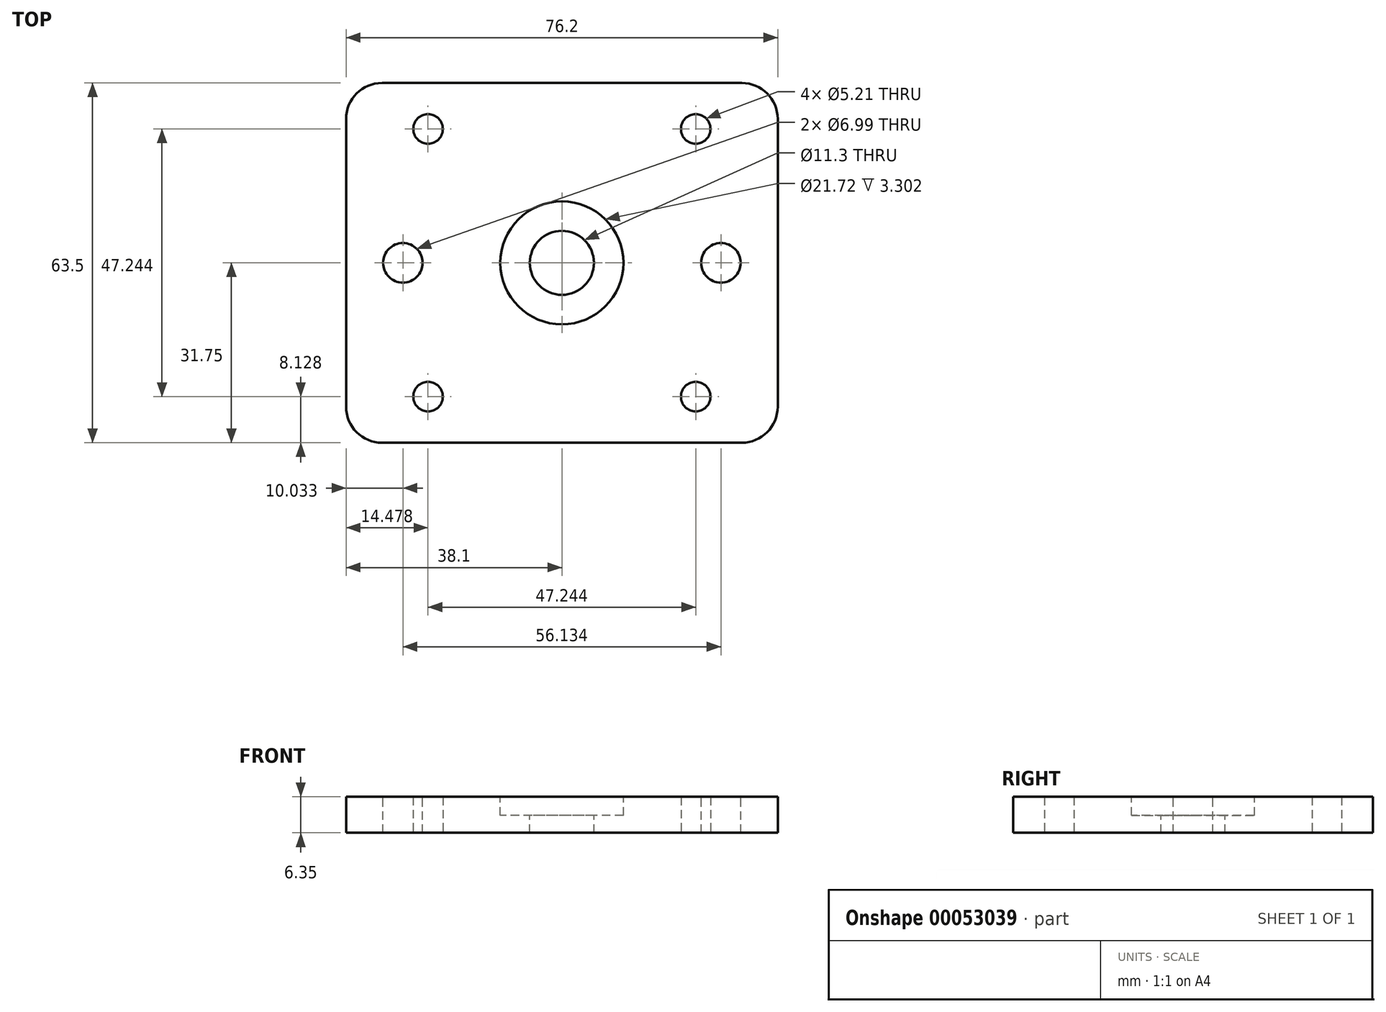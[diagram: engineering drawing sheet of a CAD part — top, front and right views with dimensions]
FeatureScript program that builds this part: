
annotation { "Feature Type Name" : "Feature", "Feature Type Description" : "" }
export const myFeature = defineFeature(function(context is Context, id is Id, definition is map)
    precondition{}
    {
        {
            var Q0;
            Q0=qCreatedBy(makeId("Top.planeOp"),FACE);
            var sketch = newSketch(context, id + "F0", { "sketchPlane" : qUnion([Q0])});
            skLineSegment(sketch, "E0.bottom", {"start": v(-23.62, 23.62) * mm, "end": v(23.62, 23.62) * mm});
            skLineSegment(sketch, "E0.top", {"start": v(-23.62, -23.62) * mm, "end": v(23.62, -23.62) * mm});
            skLineSegment(sketch, "E0.left", {"start": v(-23.62, 23.62) * mm, "end": v(-23.62, -23.62) * mm});
            skLineSegment(sketch, "E0.right", {"start": v(23.62, 23.62) * mm, "end": v(23.62, -23.62) * mm});
            skSolve(sketch);
        }
        {
            var Q0;
            Q0=qCreatedBy(makeId("Top.planeOp"),FACE);
            var sketch = newSketch(context, id + "F1", { "sketchPlane" : qUnion([Q0])});
            skLineSegment(sketch, "E1.bottom", {"start": v(-38.1, 31.75) * mm, "end": v(38.1, 31.75) * mm});
            skLineSegment(sketch, "E1.top", {"start": v(-38.1, -31.75) * mm, "end": v(38.1, -31.75) * mm});
            skLineSegment(sketch, "E1.left", {"start": v(-38.1, 31.75) * mm, "end": v(-38.1, -31.75) * mm});
            skLineSegment(sketch, "E1.right", {"start": v(38.1, 31.75) * mm, "end": v(38.1, -31.75) * mm});
            skSolve(sketch);
        }
        {
            var Q0;
            Q0=makeQuery(id+"F1.imprint","IMPRINT",FACE,{"disambiguationData":[TD([[makeQuery(id+"F1.imprint","IMPRINT",EDGE,{"derivedFrom":sQuery(id+"F1.wireOp",EDGE,"E1.bottom")}),-1.0]])]});
            extrude(context, id + "F2", {"entities" : qUnion([Q0]), "depth" : 6.35 * mm});
        }
        {
            var Q0;
            Q0=makeQuery(id+"F2.opExtrude","CAP_FACE",FACE,{"disambiguationData":[OSD([sQuery(id+"F1.wireOp",EDGE,"E1.bottom"),sQuery(id+"F1.wireOp",EDGE,"E1.top"),sQuery(id+"F1.wireOp",EDGE,"E1.left"),sQuery(id+"F1.wireOp",EDGE,"E1.right")])],"isStart":false});
            var sketch = newSketch(context, id + "F3", { "sketchPlane" : qUnion([Q0])});
            skPoint(sketch, "E2", {"position": v(0, 0) * mm});
            skSolve(sketch);
        }
        {
            var Q0;
            Q0=sQuery(id+"F3.wireOp",VERTEX,"E2");
            var Q1;
            Q1=makeQuery(id+"F2.opExtrude","SWEPT_BODY",BODY,{"disambiguationData":[OSD([sQuery(id+"F1.wireOp",EDGE,"E1.bottom"),sQuery(id+"F1.wireOp",EDGE,"E1.top"),sQuery(id+"F1.wireOp",EDGE,"E1.left"),sQuery(id+"F1.wireOp",EDGE,"E1.right")])]});
            hole(context, id + "F4", {"style" : HoleStyle.C_BORE, "holeDiameter" : 11.3 * mm, "cBoreDiameter" : 21.72 * mm, "cBoreDepth" : 3.3 * mm, "endStyle" : HoleEndStyle.THROUGH, "locations" : qUnion([Q0]), "scope" : qUnion([Q1])});
        }
        {
            var Q0;
            Q0=makeQuery(id+"F2.opExtrude","CAP_FACE",FACE,{"disambiguationData":[OSD([sQuery(id+"F1.wireOp",EDGE,"E1.bottom"),sQuery(id+"F1.wireOp",EDGE,"E1.top"),sQuery(id+"F1.wireOp",EDGE,"E1.left"),sQuery(id+"F1.wireOp",EDGE,"E1.right")])],"isStart":false});
            var sketch = newSketch(context, id + "F5", { "sketchPlane" : qUnion([Q0])});
            skCircle(sketch, "E3", {"center": v(-28.07, 0) * mm, "radius": 3.5 * mm});
            skCircle(sketch, "E4", {"center": v(28.07, 0) * mm, "radius": 3.5 * mm});
            skSolve(sketch);
        }
        {
            var Q0;
            Q0=sQuery(id+"F5.wireOp",VERTEX,"E3.center");
            var Q1;
            Q1=makeQuery(id+"F2.opExtrude","SWEPT_BODY",BODY,{"disambiguationData":[OSD([sQuery(id+"F1.wireOp",EDGE,"E1.bottom"),sQuery(id+"F1.wireOp",EDGE,"E1.top"),sQuery(id+"F1.wireOp",EDGE,"E1.left"),sQuery(id+"F1.wireOp",EDGE,"E1.right")])]});
            hole(context, id + "F6", {"style" : HoleStyle.SIMPLE, "holeDiameter" : 7 * mm, "endStyle" : HoleEndStyle.THROUGH, "locations" : qUnion([Q0]), "scope" : qUnion([Q1])});
        }
        {
            var Q0;
            Q0=sQuery(id+"F5.wireOp",VERTEX,"E4.center");
            var Q1;
            Q1=makeQuery(id+"F2.opExtrude","SWEPT_BODY",BODY,{"disambiguationData":[OSD([sQuery(id+"F1.wireOp",EDGE,"E1.bottom"),sQuery(id+"F1.wireOp",EDGE,"E1.top"),sQuery(id+"F1.wireOp",EDGE,"E1.left"),sQuery(id+"F1.wireOp",EDGE,"E1.right")])]});
            hole(context, id + "F7", {"style" : HoleStyle.SIMPLE, "holeDiameter" : 7 * mm, "endStyle" : HoleEndStyle.THROUGH, "locations" : qUnion([Q0]), "scope" : qUnion([Q1])});
        }
        {
            var Q0;
            Q0=sQuery(id+"F0.wireOp",VERTEX,"E0.left.start");
            var Q1;
            Q1=makeQuery(id+"F2.opExtrude","SWEPT_BODY",BODY,{"disambiguationData":[OSD([sQuery(id+"F1.wireOp",EDGE,"E1.bottom"),sQuery(id+"F1.wireOp",EDGE,"E1.top"),sQuery(id+"F1.wireOp",EDGE,"E1.left"),sQuery(id+"F1.wireOp",EDGE,"E1.right")])]});
            hole(context, id + "F8", {"style" : HoleStyle.SIMPLE, "holeDiameter" : 5.2 * mm, "endStyle" : HoleEndStyle.THROUGH, "oppositeDirection" : true, "locations" : qUnion([Q0]), "scope" : qUnion([Q1])});
        }
        {
            var Q0;
            Q0=sQuery(id+"F0.wireOp",VERTEX,"E0.right.start");
            var Q1;
            Q1=sQuery(id+"F0.wireOp",VERTEX,"E0.left.end");
            var Q2;
            Q2=makeQuery(id+"F2.opExtrude","SWEPT_BODY",BODY,{"disambiguationData":[OSD([sQuery(id+"F1.wireOp",EDGE,"E1.bottom"),sQuery(id+"F1.wireOp",EDGE,"E1.top"),sQuery(id+"F1.wireOp",EDGE,"E1.left"),sQuery(id+"F1.wireOp",EDGE,"E1.right")])]});
            hole(context, id + "F9", {"style" : HoleStyle.SIMPLE, "holeDiameter" : 5.2 * mm, "endStyle" : HoleEndStyle.THROUGH, "oppositeDirection" : true, "locations" : qUnion([Q0, Q1]), "scope" : qUnion([Q2])});
        }
        {
            var Q0;
            Q0=sQuery(id+"F0.wireOp",VERTEX,"E0.right.end");
            var Q1;
            Q1=makeQuery(id+"F2.opExtrude","SWEPT_BODY",BODY,{"disambiguationData":[OSD([sQuery(id+"F1.wireOp",EDGE,"E1.bottom"),sQuery(id+"F1.wireOp",EDGE,"E1.top"),sQuery(id+"F1.wireOp",EDGE,"E1.left"),sQuery(id+"F1.wireOp",EDGE,"E1.right")])]});
            hole(context, id + "F10", {"style" : HoleStyle.SIMPLE, "holeDiameter" : 5.2 * mm, "endStyle" : HoleEndStyle.THROUGH, "oppositeDirection" : true, "locations" : qUnion([Q0]), "scope" : qUnion([Q1])});
        }
        {
            var Q0;
            Q0=makeQuery(id+"F2.opExtrude","SWEPT_EDGE",EDGE,{"disambiguationData":[OSD([sQuery(id+"F1.wireOp",EDGE,"E1.top"),sQuery(id+"F1.wireOp",EDGE,"E1.left")])]});
            var Q1;
            Q1=makeQuery(id+"F2.opExtrude","SWEPT_EDGE",EDGE,{"disambiguationData":[OSD([sQuery(id+"F1.wireOp",EDGE,"E1.top"),sQuery(id+"F1.wireOp",EDGE,"E1.right")])]});
            var Q2;
            Q2=makeQuery(id+"F2.opExtrude","SWEPT_EDGE",EDGE,{"disambiguationData":[OSD([sQuery(id+"F1.wireOp",EDGE,"E1.bottom"),sQuery(id+"F1.wireOp",EDGE,"E1.right")])]});
            var Q3;
            Q3=makeQuery(id+"F2.opExtrude","SWEPT_EDGE",EDGE,{"disambiguationData":[OSD([sQuery(id+"F1.wireOp",EDGE,"E1.bottom"),sQuery(id+"F1.wireOp",EDGE,"E1.left")])]});
            fillet(context, id + "F11", {"entities" : qUnion([Q0, Q1, Q2, Q3]), "radius" : 6.35 * mm, "tangentPropagation" : true, "allowEdgeOverflow" : false});
        }
    });
